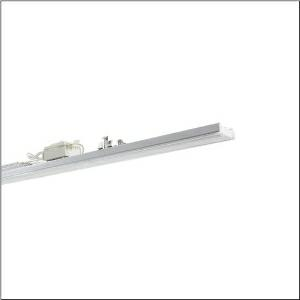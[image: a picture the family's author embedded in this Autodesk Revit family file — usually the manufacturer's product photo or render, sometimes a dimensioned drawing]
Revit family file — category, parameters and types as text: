
# Revit family: licross_r__21_recessed_ho_52te1edv4lxs_3477
name_source: partatom
category: Lighting Fixtures
units: mm (PartAtom-declared; Revit-internal decimal feet)

## family parameters
Cut with Voids When Loaded = No
Host = Face
Light Source = No
Part Type = Normal
Room Calculation Point = No
Round Connector Dimension = Use Diameter
Shared = No

## types (1)
- --- (1 x LED, 20000 lm, 112.9 W, 4000K)
    Apparent Load = 113 VA
    CIE Flux Codes = 85 95 99 100 100
    Color Rendering = 80
    Color Temperature = 4000K
    Default Elevation = 1800 mm
    Description = Licross® 21 Recessed HO, luminaire insert, of sheet steel, galvanised, coil coated, white, length: 2.250mm, width: 66mm, height: 67mm, LED rated luminous flux: 20.000lm, light colour: 840, control gear: DALI 2, with plug, 5-pole, with phase selection, mains connection: 220..240V, AC, 50/60Hz, rated input power: 113W, halogen-free wiring, primary light control with lens, of plastic, primary optical cover: cover, of PMMA, light emission: direct distribution, primary light characteristic: symmetric, protection rating (complete): IP54, insulation class (complete): insulation class I (protective earthing), certification: CE, ENEC, VDE, UKCA, protection symbol: D if used in an environment with non-conductive dust loads with corresponding accessories, impact resistance: IK06, permissible ambient temperature for indoor applications: -40..+35°C, corresponds to IFS (International Featured Standards) requirements for safety and quality in the food industry, reducing of maximum allowable ambient temperature of 5°C with ceiling mounting, LABS conformity tested according to VDMA 24364:2018-05, packaging unit: 1 piece
    Height = 58 mm
    Lamp = 1 x LED
    Lamp Light Flux = 20000 lm
    Lamp Power = 112.9 W
    Lamp count = 1
    Length = 2250 mm
    Luminous efficacy = 177 lm/W
    Manufacturer = Siteco
    ModVariant = No
    Model = 52TE1EDV4LXS
    Mounting Place = Ceiling
    Mounting Type = Pendant
    Number of Poles = 1
    OnlyDefault = Yes
    Power Factor = 1
    Product Name = Licross® 21 Recessed HO
    Product group = luminaire insert
    ProductGroupID = 902
    Protection Class = Protection class I
    Protection Degree = IP 54
    RLX_Detail_Level = 1
    RLX_Emergency_Light_Flux = 0 lm
    RLX_Emergency_Type = 0
    RLX_Emergency_Type_DB = No
    RlxData = <blob elided: 29345 chars, md5=67a5f8b2>
    Socket = socket
    Standby Power = 0 W
    System Light Flux = 20000 lm
    System Power = 113 W
    Type Comments = factory setting: luminous flux: 100 % | dim-lin: 254 | 438 mA
    Type Image = l_1296930.jpg
    URL = http://relux.com
    VarID = @adj_125380
    Voltage = 0 V
    Weight = 0.00 kg
    Width = 66 mm

## geometry (parser evidence)
native form markers: Blend x4, Sweep x11
no freeform markers — native parametric forms only
